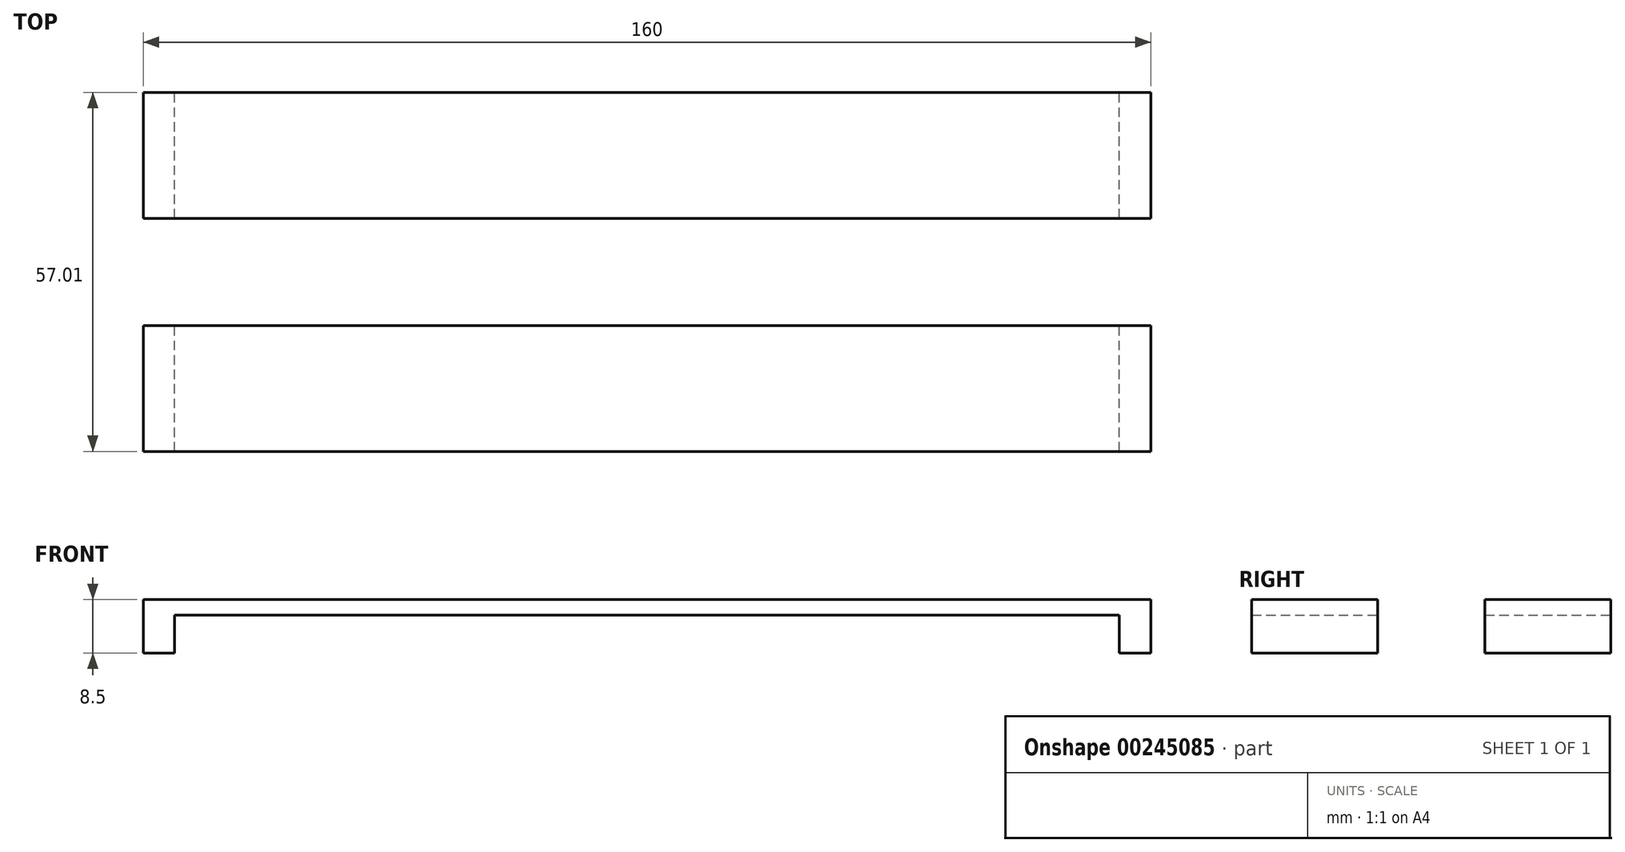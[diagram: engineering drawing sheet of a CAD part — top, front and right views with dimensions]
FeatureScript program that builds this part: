
annotation { "Feature Type Name" : "Feature", "Feature Type Description" : "" }
export const myFeature = defineFeature(function(context is Context, id is Id, definition is map)
    precondition{}
    {
        {
            var Q0;
            Q0=qCreatedBy(makeId("Top.planeOp"),FACE);
            var sketch = newSketch(context, id + "F0", { "sketchPlane" : qUnion([Q0])});
            skLineSegment(sketch, "E0.bottom", {"start": v(-80, 10) * mm, "end": v(80, 10) * mm});
            skLineSegment(sketch, "E0.top", {"start": v(-80, -10) * mm, "end": v(80, -10) * mm});
            skLineSegment(sketch, "E0.left", {"start": v(-80, 10) * mm, "end": v(-80, -10) * mm});
            skLineSegment(sketch, "E0.right", {"start": v(80, 10) * mm, "end": v(80, -10) * mm});
            skPoint(sketch, "E0.middle", {"position": v(0, 0) * mm});
            skSolve(sketch);
        }
        {
            var Q0;
            Q0=makeQuery(id+"F0.imprint","IMPRINT",FACE,{"disambiguationData":[TD([[makeQuery(id+"F0.imprint","IMPRINT",EDGE,{"derivedFrom":sQuery(id+"F0.wireOp",EDGE,"E0.bottom")}),-1.0]])]});
            extrude(context, id + "F1", {"entities" : qUnion([Q0]), "oppositeDirection" : true, "depth" : 2.5 * mm});
        }
        {
            var Q0;
            Q0=makeQuery(id+"F1.opExtrude","CAP_FACE",FACE,{"disambiguationData":[OSD([sQuery(id+"F0.wireOp",EDGE,"E0.bottom"),sQuery(id+"F0.wireOp",EDGE,"E0.top"),sQuery(id+"F0.wireOp",EDGE,"E0.left"),sQuery(id+"F0.wireOp",EDGE,"E0.right")])],"isStart":false});
            var sketch = newSketch(context, id + "F2", { "sketchPlane" : qUnion([Q0])});
            skLineSegment(sketch, "E1", {"start": v(80, 10) * mm, "end": v(75, 10) * mm});
            skLineSegment(sketch, "E2", {"start": v(75, 10) * mm, "end": v(75, -10) * mm});
            skLineSegment(sketch, "E3", {"start": v(75, -10) * mm, "end": v(80, -10) * mm});
            skLineSegment(sketch, "E4", {"start": v(80, -10) * mm, "end": v(80, 10) * mm});
            skLineSegment(sketch, "E5", {"start": v(-80, 10) * mm, "end": v(-75, 10) * mm});
            skLineSegment(sketch, "E6", {"start": v(-75, 10) * mm, "end": v(-75, -10) * mm});
            skLineSegment(sketch, "E7", {"start": v(-75, -10) * mm, "end": v(-80, -10) * mm});
            skLineSegment(sketch, "E8", {"start": v(-80, -10) * mm, "end": v(-80, 10) * mm});
            skSolve(sketch);
        }
        {
            var Q0;
            Q0=makeQuery(id+"F2.imprint","IMPRINT",FACE,{"disambiguationData":[TD([[makeQuery(id+"F2.imprint","IMPRINT",EDGE,{"derivedFrom":sQuery(id+"F2.wireOp",EDGE,"E5")}),-1.0]])]});
            var Q1;
            Q1=makeQuery(id+"F2.imprint","IMPRINT",FACE,{"disambiguationData":[TD([[makeQuery(id+"F2.imprint","IMPRINT",EDGE,{"derivedFrom":sQuery(id+"F2.wireOp",EDGE,"E1")}),-1.0]])]});
            extrude(context, id + "F3", {"entities" : qUnion([Q0, Q1]), "operationType" : NewBodyOperationType.ADD, "depth" : 6 * mm});
        }
        {
            var Q0;
            Q0=qCreatedBy(makeId("Top.planeOp"),FACE);
            var sketch = newSketch(context, id + "F4", { "sketchPlane" : qUnion([Q0])});
            skLineSegment(sketch, "E9.bottom", {"start": v(-80, 47.01) * mm, "end": v(80, 47.01) * mm});
            skLineSegment(sketch, "E9.top", {"start": v(-80, 27.01) * mm, "end": v(80, 27.01) * mm});
            skLineSegment(sketch, "E9.left", {"start": v(-80, 47.01) * mm, "end": v(-80, 27.01) * mm});
            skLineSegment(sketch, "E9.right", {"start": v(80, 47.01) * mm, "end": v(80, 27.01) * mm});
            skPoint(sketch, "E9.middle", {"position": v(0, 37.01) * mm});
            skSolve(sketch);
        }
        {
            var Q0;
            Q0=makeQuery(id+"F4.imprint","IMPRINT",FACE,{"disambiguationData":[TD([[makeQuery(id+"F4.imprint","IMPRINT",EDGE,{"derivedFrom":sQuery(id+"F4.wireOp",EDGE,"E9.bottom")}),-1.0]])]});
            extrude(context, id + "F5", {"entities" : qUnion([Q0]), "oppositeDirection" : true, "depth" : 2.5 * mm});
        }
        {
            var Q0;
            Q0=makeQuery(id+"F5.opExtrude","CAP_FACE",FACE,{"disambiguationData":[OSD([sQuery(id+"F4.wireOp",EDGE,"E9.bottom"),sQuery(id+"F4.wireOp",EDGE,"E9.top"),sQuery(id+"F4.wireOp",EDGE,"E9.left"),sQuery(id+"F4.wireOp",EDGE,"E9.right")])],"isStart":false});
            var sketch = newSketch(context, id + "F6", { "sketchPlane" : qUnion([Q0])});
            skLineSegment(sketch, "E10", {"start": v(80, -27.01) * mm, "end": v(75, -27.01) * mm});
            skLineSegment(sketch, "E11", {"start": v(75, -27.01) * mm, "end": v(75, -47.01) * mm});
            skLineSegment(sketch, "E12", {"start": v(75, -47.01) * mm, "end": v(80, -47.01) * mm});
            skLineSegment(sketch, "E13", {"start": v(80, -47.01) * mm, "end": v(80, -27.01) * mm});
            skLineSegment(sketch, "E14", {"start": v(-80, -27.01) * mm, "end": v(-75, -27.01) * mm});
            skLineSegment(sketch, "E15", {"start": v(-75, -27.01) * mm, "end": v(-75, -47.01) * mm});
            skLineSegment(sketch, "E16", {"start": v(-75, -47.01) * mm, "end": v(-80, -47.01) * mm});
            skLineSegment(sketch, "E17", {"start": v(-80, -47.01) * mm, "end": v(-80, -27.01) * mm});
            skSolve(sketch);
        }
        {
            var Q0;
            Q0=makeQuery(id+"F6.imprint","IMPRINT",FACE,{"disambiguationData":[TD([[makeQuery(id+"F6.imprint","IMPRINT",EDGE,{"derivedFrom":sQuery(id+"F6.wireOp",EDGE,"E14")}),-1.0]])]});
            var Q1;
            Q1=makeQuery(id+"F6.imprint","IMPRINT",FACE,{"disambiguationData":[TD([[makeQuery(id+"F6.imprint","IMPRINT",EDGE,{"derivedFrom":sQuery(id+"F6.wireOp",EDGE,"E10")}),-1.0]])]});
            extrude(context, id + "F7", {"entities" : qUnion([Q0, Q1]), "operationType" : NewBodyOperationType.ADD, "depth" : 6 * mm});
        }
    });
